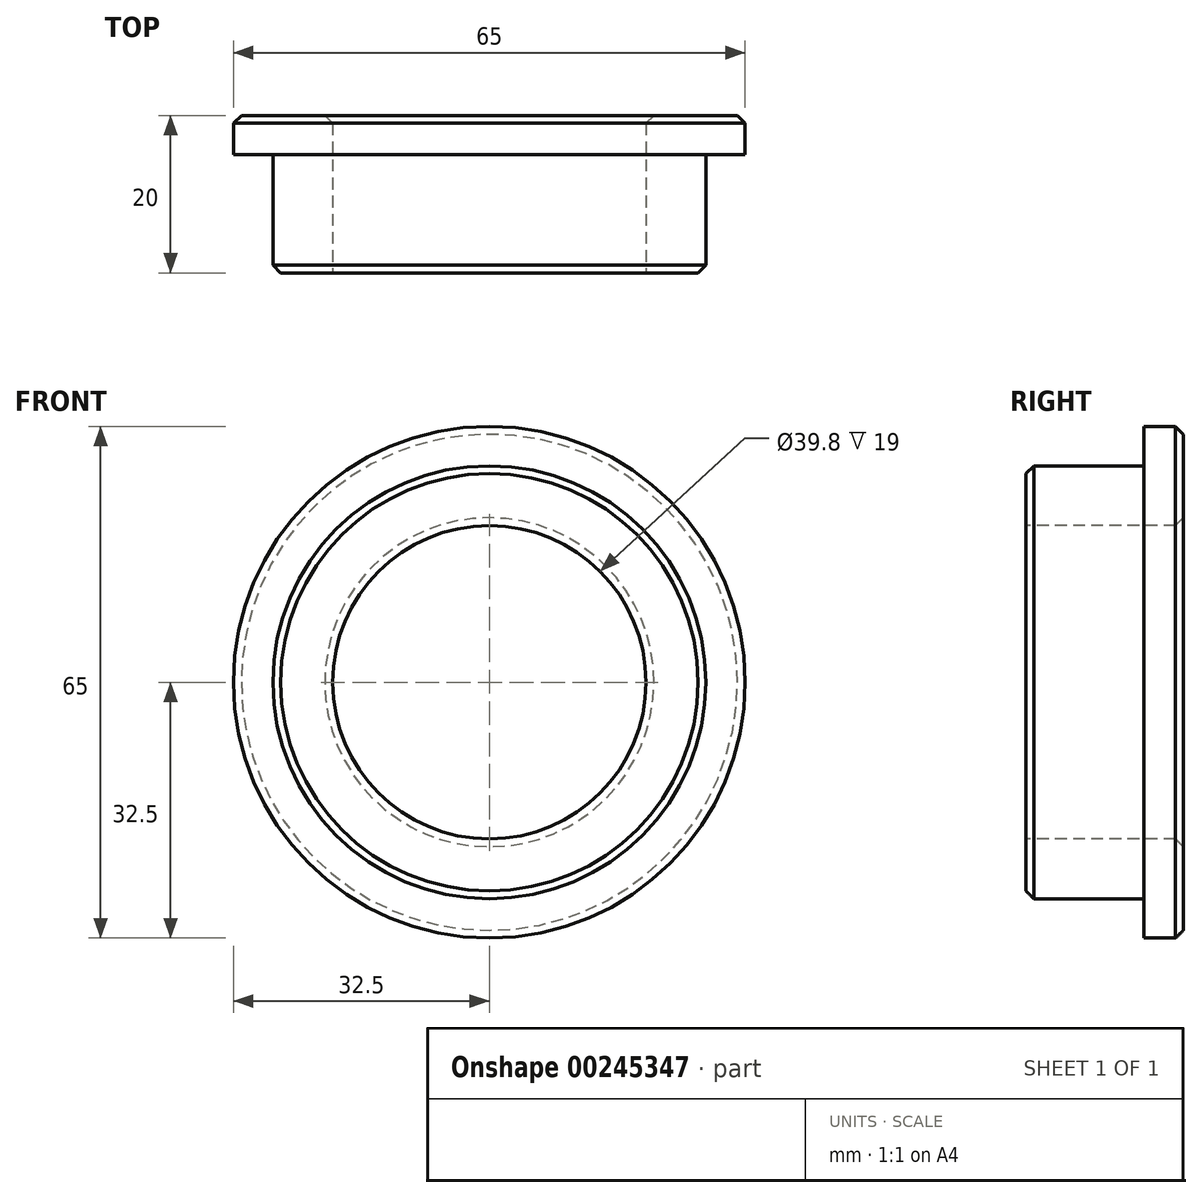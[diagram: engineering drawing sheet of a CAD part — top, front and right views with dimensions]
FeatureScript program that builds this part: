
annotation { "Feature Type Name" : "Feature", "Feature Type Description" : "" }
export const myFeature = defineFeature(function(context is Context, id is Id, definition is map)
    precondition{}
    {
        {
            var Q0;
            Q0=qCreatedBy(makeId("Front.planeOp"),FACE);
            var sketch = newSketch(context, id + "F0", { "sketchPlane" : qUnion([Q0])});
            skCircle(sketch, "E0", {"center": v(0, 0) * mm, "radius": 32.5 * mm});
            skSolve(sketch);
        }
        {
            var Q0;
            Q0 = qSketchRegion(id + "F0", true);
            extrude(context, id + "F1", {"entities" : qUnion([Q0]), "depth" : 5 * mm});
        }
        {
            var Q0;
            Q0=makeQuery(id+"F1.opExtrude","CAP_FACE",FACE,{"disambiguationData":[OSD([sQuery(id+"F0.wireOp",EDGE,"E0")])],"isStart":false});
            var sketch = newSketch(context, id + "F2", { "sketchPlane" : qUnion([Q0])});
            skCircle(sketch, "E1", {"center": v(0, 0) * mm, "radius": 27.5 * mm});
            skSolve(sketch);
        }
        {
            var Q0;
            Q0 = qSketchRegion(id + "F2", true);
            extrude(context, id + "F3", {"entities" : qUnion([Q0]), "operationType" : NewBodyOperationType.ADD, "depth" : 15 * mm});
        }
        {
            var Q0;
            Q0=makeQuery(id+"F3.opExtrude","CAP_FACE",FACE,{"disambiguationData":[OSD([sQuery(id+"F2.wireOp",EDGE,"E1")])],"isStart":false});
            var sketch = newSketch(context, id + "F4", { "sketchPlane" : qUnion([Q0])});
            skCircle(sketch, "E2", {"center": v(0, 0) * mm, "radius": 19.9 * mm});
            skSolve(sketch);
        }
        {
            var Q0;
            Q0 = qSketchRegion(id + "F4", true);
            extrude(context, id + "F5", {"entities" : qUnion([Q0]), "operationType" : NewBodyOperationType.REMOVE, "oppositeDirection" : true, "depth" : 25 * mm});
        }
        {
            var Q0;
            Q0=makeQuery(id+"F1.opExtrude","CAP_EDGE",EDGE,{"disambiguationData":[OSD([sQuery(id+"F0.wireOp",EDGE,"E0")])],"isStart":true});
            var Q1;
            Q1=makeQuery(id+"F3.opExtrude","CAP_EDGE",EDGE,{"disambiguationData":[OSD([sQuery(id+"F2.wireOp",EDGE,"E1")])],"isStart":false});
            var Q2;
            Q2=makeQuery(id+"F5.boolean.opBoolean","COPY",EDGE,{"derivedFrom":makeQuery(id+"F5.opExtrude","CAP_EDGE",EDGE,{"disambiguationData":[OSD([sQuery(id+"F4.wireOp",EDGE,"E2")])],"isStart":true})});
            var Q3;
            Q3=makeQuery(id+"F5.boolean.opBoolean","INTERSECT",EDGE,{"derivedFrom":[makeQuery(id+"F1.opExtrude","CAP_FACE",FACE,{"disambiguationData":[OSD([sQuery(id+"F0.wireOp",EDGE,"E0")])],"isStart":true}),makeQuery(id+"F5.opExtrude","SWEPT_FACE",FACE,{"disambiguationData":[OSD([sQuery(id+"F4.wireOp",EDGE,"E2")])]})]});
            chamfer(context, id + "F6", {"entities" : qUnion([Q0, Q1, Q2, Q3]), "width" : 1 * mm, "tangentPropagation" : true});
        }
    });
